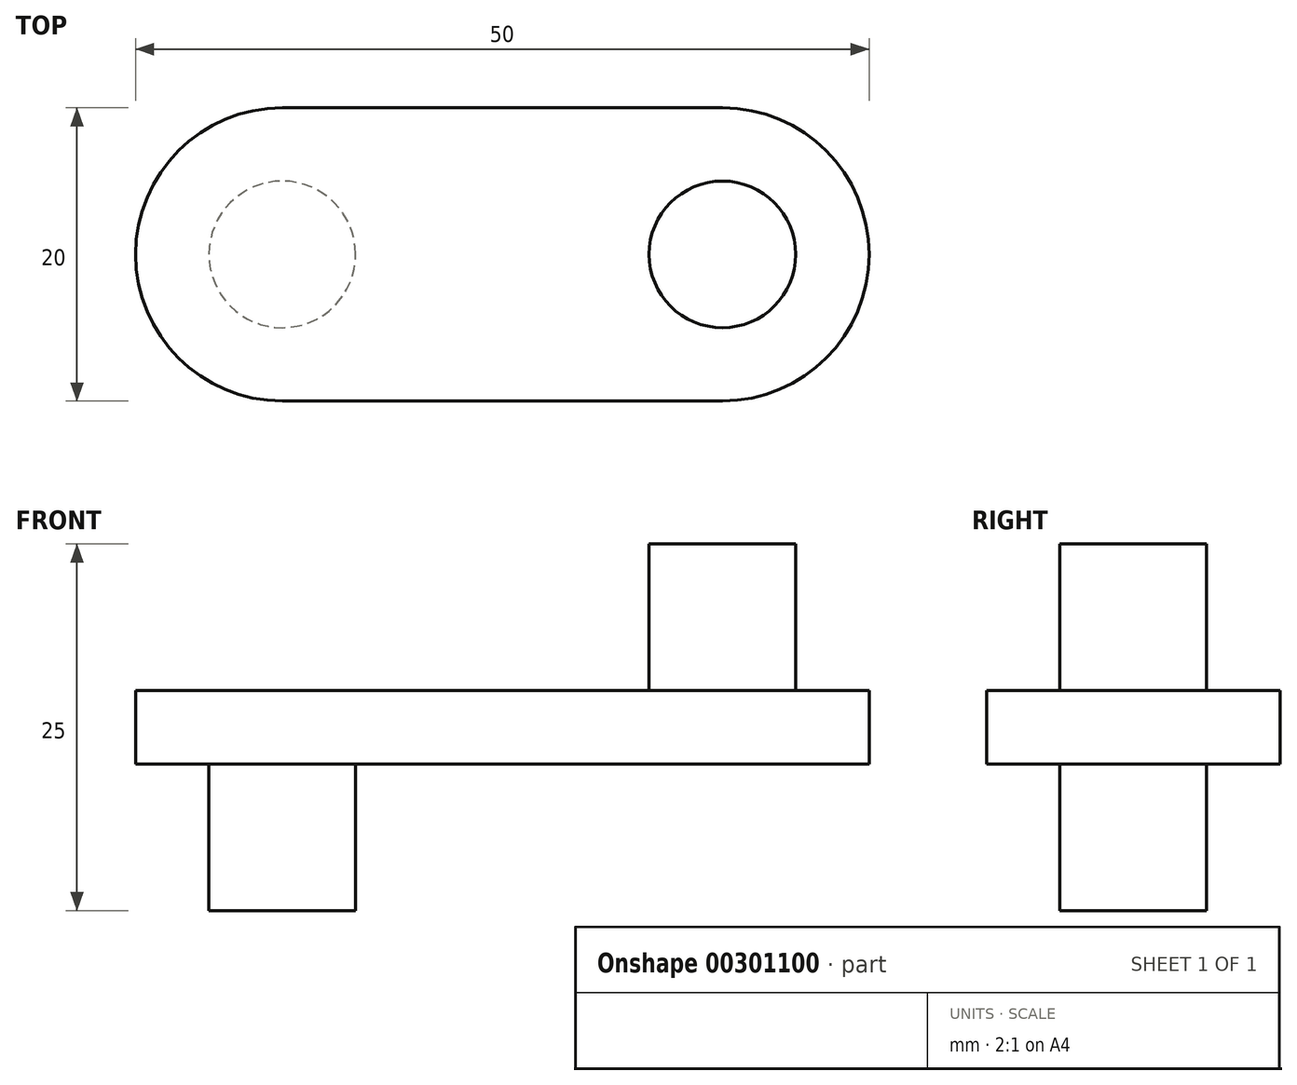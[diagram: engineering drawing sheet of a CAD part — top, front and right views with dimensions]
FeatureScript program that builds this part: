
annotation { "Feature Type Name" : "Feature", "Feature Type Description" : "" }
export const myFeature = defineFeature(function(context is Context, id is Id, definition is map)
    precondition{}
    {
        {
            var Q0;
            Q0=qCreatedBy(makeId("Top.planeOp"),FACE);
            var sketch = newSketch(context, id + "F0", { "sketchPlane" : qUnion([Q0])});
            skLineSegment(sketch, "E0", {"start": v(-14.49, 30) * mm, "end": v(15.51, 30) * mm});
            skLineSegment(sketch, "E1", {"start": v(-14.49, 10) * mm, "end": v(15.51, 10) * mm});
            skArc(sketch, "E2", {"start": v(-14.49, 30) * mm, "mid": v(-24.49, 20) * mm, "end": v(-14.49, 10) * mm});
            skArc(sketch, "E3", {"start": v(15.51, 30) * mm, "mid": v(25.51, 20) * mm, "end": v(15.51, 10) * mm});
            skSolve(sketch);
        }
        {
            var Q0;
            Q0=makeQuery(id+"F0.imprint","IMPRINT",FACE,{"disambiguationData":[TD([[makeQuery(id+"F0.imprint","IMPRINT",EDGE,{"derivedFrom":sQuery(id+"F0.wireOp",EDGE,"E0")}),-1.0]])]});
            extrude(context, id + "F1", {"entities" : qUnion([Q0]), "depth" : 5 * mm});
        }
        {
            var Q0;
            {var subQ0=sQuery(id+"F0.wireOp",EDGE,"mBLVDeMJ-yPQI-Pzb1-PrSd-Bz4JsfYyK7wo");Q0=makeQuery(id+"F4DjID189QdfSn4_0.boolean.opBoolean","MERGE",FACE,{"derivedFrom":[makeQuery(id+"F1.opExtrude","CAP_FACE",FACE,{"disambiguationData":[OSD([sQuery(id+"F0.wireOp",EDGE,"E0"),sQuery(id+"F0.wireOp",EDGE,"E1"),sQuery(id+"F0.wireOp",EDGE,"E2"),sQuery(id+"F0.wireOp",EDGE,"E3"),subQ0])],"isStart":true}),makeQuery(id+"F4DjID189QdfSn4_0.opExtrude","CAP_FACE",FACE,{"disambiguationData":[OSD([subQ0])],"isStart":true})]});}
            var sketch = newSketch(context, id + "F2", { "sketchPlane" : qUnion([Q0])});
            skCircle(sketch, "E4", {"center": v(-14.49, -20) * mm, "radius": 5 * mm});
            skSolve(sketch);
        }
        {
            var Q0;
            Q0=makeQuery(id+"F2.imprint","IMPRINT",FACE,{"disambiguationData":[TD([[makeQuery(id+"F2.imprint","IMPRINT",EDGE,{"derivedFrom":sQuery(id+"F2.wireOp",EDGE,"E4")}),1.0]])]});
            extrude(context, id + "F3", {"entities" : qUnion([Q0]), "operationType" : NewBodyOperationType.ADD, "depth" : 10 * mm});
        }
        {
            var Q0;
            Q0=makeQuery(id+"F1.opExtrude","CAP_FACE",FACE,{"disambiguationData":[OSD([sQuery(id+"F0.wireOp",EDGE,"E0"),sQuery(id+"F0.wireOp",EDGE,"E1"),sQuery(id+"F0.wireOp",EDGE,"E2"),sQuery(id+"F0.wireOp",EDGE,"E3")])],"isStart":false});
            var sketch = newSketch(context, id + "F4", { "sketchPlane" : qUnion([Q0])});
            skCircle(sketch, "E5", {"center": v(15.51, 20) * mm, "radius": 5 * mm});
            skSolve(sketch);
        }
        {
            var Q0;
            Q0=makeQuery(id+"F4.imprint","IMPRINT",FACE,{"disambiguationData":[TD([[makeQuery(id+"F4.imprint","IMPRINT",EDGE,{"derivedFrom":sQuery(id+"F4.wireOp",EDGE,"E5")}),1.0]])]});
            extrude(context, id + "F5", {"entities" : qUnion([Q0]), "operationType" : NewBodyOperationType.ADD, "depth" : 10 * mm});
        }
    });
